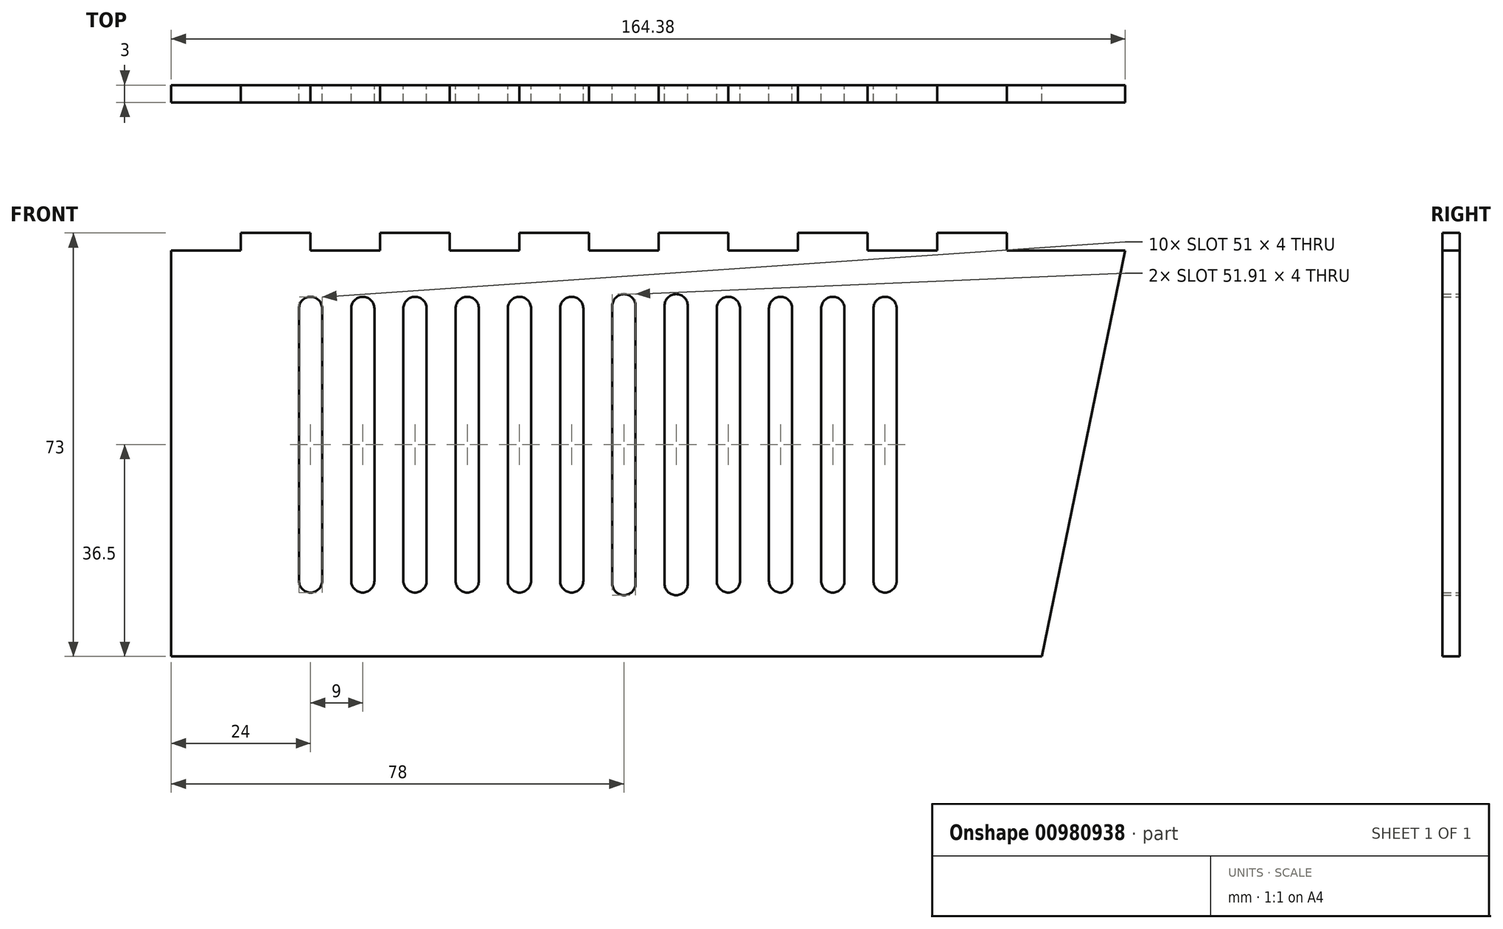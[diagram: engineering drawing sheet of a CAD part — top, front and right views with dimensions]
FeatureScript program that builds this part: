
annotation { "Feature Type Name" : "Feature", "Feature Type Description" : "" }
export const myFeature = defineFeature(function(context is Context, id is Id, definition is map)
    precondition{}
    {
        {
            var Q0;
            Q0=qCreatedBy(makeId("Front.planeOp"),FACE);
            var sketch = newSketch(context, id + "F0", { "sketchPlane" : qUnion([Q0])});
            skLineSegment(sketch, "E0.bottom", {"start": v(67.5, -36.5) * mm, "end": v(-82.5, -36.5) * mm});
            skPoint(sketch, "E0.middle", {"position": v(0, 0) * mm});
            skLineSegment(sketch, "E1", {"start": v(81.88, 33.5) * mm, "end": v(67.5, -36.5) * mm});
            skPoint(sketch, "E0.left.start.orphan", {"position": v(85.5, -36.5) * mm});
            skLineSegment(sketch, "E2", {"start": v(-82.5, -36.5) * mm, "end": v(-82.5, 33.5) * mm});
            skLineSegment(sketch, "E3", {"start": v(-82.5, 33.5) * mm, "end": v(-70.5, 33.5) * mm});
            skLineSegment(sketch, "E4", {"start": v(-70.5, 33.5) * mm, "end": v(-70.5, 36.5) * mm});
            skLineSegment(sketch, "E5", {"start": v(-70.5, 36.5) * mm, "end": v(-58.5, 36.5) * mm});
            skLineSegment(sketch, "E6", {"start": v(-58.5, 36.5) * mm, "end": v(-58.5, 33.5) * mm});
            skLineSegment(sketch, "E7", {"start": v(-58.5, 33.5) * mm, "end": v(-46.5, 33.5) * mm});
            skLineSegment(sketch, "E8.1.0.1", {"start": v(-34.5, 33.5) * mm, "end": v(-22.5, 33.5) * mm});
            skLineSegment(sketch, "E8.1.0.2", {"start": v(-46.5, 36.5) * mm, "end": v(-34.5, 36.5) * mm});
            skLineSegment(sketch, "E8.1.0.3", {"start": v(-46.5, 33.5) * mm, "end": v(-46.5, 36.5) * mm});
            skLineSegment(sketch, "E8.1.0.4", {"start": v(-34.5, 36.5) * mm, "end": v(-34.5, 33.5) * mm});
            skLineSegment(sketch, "E8.2.0.0", {"start": v(-34.5, 33.5) * mm, "end": v(-22.5, 33.5) * mm});
            skLineSegment(sketch, "E8.2.0.1", {"start": v(-10.5, 33.5) * mm, "end": v(1.5, 33.5) * mm});
            skLineSegment(sketch, "E8.2.0.2", {"start": v(-22.5, 36.5) * mm, "end": v(-10.5, 36.5) * mm});
            skLineSegment(sketch, "E8.2.0.3", {"start": v(-22.5, 33.5) * mm, "end": v(-22.5, 36.5) * mm});
            skLineSegment(sketch, "E8.2.0.4", {"start": v(-10.5, 36.5) * mm, "end": v(-10.5, 33.5) * mm});
            skLineSegment(sketch, "E8.3.0.0", {"start": v(-10.5, 33.5) * mm, "end": v(1.5, 33.5) * mm});
            skLineSegment(sketch, "E8.3.0.1", {"start": v(13.5, 33.5) * mm, "end": v(25.5, 33.5) * mm});
            skLineSegment(sketch, "E8.3.0.2", {"start": v(1.5, 36.5) * mm, "end": v(13.5, 36.5) * mm});
            skLineSegment(sketch, "E8.3.0.3", {"start": v(1.5, 33.5) * mm, "end": v(1.5, 36.5) * mm});
            skLineSegment(sketch, "E8.3.0.4", {"start": v(13.5, 36.5) * mm, "end": v(13.5, 33.5) * mm});
            skLineSegment(sketch, "E8.4.0.0", {"start": v(13.5, 33.5) * mm, "end": v(25.5, 33.5) * mm});
            skLineSegment(sketch, "E8.4.0.1", {"start": v(37.5, 33.5) * mm, "end": v(49.5, 33.5) * mm});
            skLineSegment(sketch, "E8.4.0.2", {"start": v(25.5, 36.5) * mm, "end": v(37.5, 36.5) * mm});
            skLineSegment(sketch, "E8.4.0.3", {"start": v(25.5, 33.5) * mm, "end": v(25.5, 36.5) * mm});
            skLineSegment(sketch, "E8.4.0.4", {"start": v(37.5, 36.5) * mm, "end": v(37.5, 33.5) * mm});
            skLineSegment(sketch, "E8.5.0.0", {"start": v(37.5, 33.5) * mm, "end": v(49.5, 33.5) * mm});
            skLineSegment(sketch, "E8.5.0.2", {"start": v(49.5, 36.5) * mm, "end": v(61.5, 36.5) * mm});
            skLineSegment(sketch, "E8.5.0.3", {"start": v(49.5, 33.5) * mm, "end": v(49.5, 36.5) * mm});
            skLineSegment(sketch, "E8.5.0.4", {"start": v(61.5, 36.5) * mm, "end": v(61.5, 33.5) * mm});
            skLineSegment(sketch, "E8.direction1", {"start": v(-82.5, 33.5) * mm, "end": v(-70.5, 33.5) * mm, "construction": true});
            skLineSegment(sketch, "E9", {"start": v(61.5, 33.5) * mm, "end": v(81.88, 33.5) * mm});
            skPoint(sketch, "E10.orphan", {"position": v(82.5, 36.5) * mm});
            skPoint(sketch, "E11.orphan", {"position": v(82.5, 33.5) * mm});
            skPoint(sketch, "E12.orphan", {"position": v(-82.5, 36.5) * mm});
            skLineSegment(sketch, "E13.left", {"start": v(-38.5, 23.5) * mm, "end": v(-38.5, -23.5) * mm});
            skLineSegment(sketch, "E13.right", {"start": v(-42.5, 23.5) * mm, "end": v(-42.5, -23.5) * mm});
            skPoint(sketch, "E13.middle", {"position": v(-40.5, 0) * mm});
            skLineSegment(sketch, "E14.left", {"start": v(-29.5, -23.5) * mm, "end": v(-29.5, 23.5) * mm});
            skLineSegment(sketch, "E14.right", {"start": v(-33.5, -23.5) * mm, "end": v(-33.5, 23.5) * mm});
            skPoint(sketch, "E14.middle", {"position": v(-31.5, 0) * mm});
            skLineSegment(sketch, "E15.left", {"start": v(-20.5, -23.5) * mm, "end": v(-20.5, 23.5) * mm});
            skLineSegment(sketch, "E15.right", {"start": v(-24.5, -23.5) * mm, "end": v(-24.5, 23.5) * mm});
            skPoint(sketch, "E15.middle", {"position": v(-22.5, 0) * mm});
            skLineSegment(sketch, "E16.left", {"start": v(-11.5, -23.5) * mm, "end": v(-11.5, 23.5) * mm});
            skLineSegment(sketch, "E16.right", {"start": v(-15.5, -23.5) * mm, "end": v(-15.5, 23.5) * mm});
            skPoint(sketch, "E16.middle", {"position": v(-13.5, 0) * mm});
            skLineSegment(sketch, "E17.left", {"start": v(-2.5, -23.95) * mm, "end": v(-2.5, 23.95) * mm});
            skLineSegment(sketch, "E17.right", {"start": v(-6.5, -23.95) * mm, "end": v(-6.5, 23.95) * mm});
            skPoint(sketch, "E17.middle", {"position": v(-4.5, 0) * mm});
            skLineSegment(sketch, "E18.MirrorCS", {"start": v(24.5, -23.5) * mm, "end": v(24.5, 23.5) * mm});
            skPoint(sketch, "E19.MirrorP", {"position": v(22.5, 0) * mm});
            skPoint(sketch, "E20.MirrorP", {"position": v(13.5, 0) * mm});
            skLineSegment(sketch, "E21.MirrorCS", {"start": v(20.5, -23.5) * mm, "end": v(20.5, 23.5) * mm});
            skLineSegment(sketch, "E22.MirrorCS", {"start": v(29.5, -23.5) * mm, "end": v(29.5, 23.5) * mm});
            skLineSegment(sketch, "E23.MirrorCS", {"start": v(6.5, -23.95) * mm, "end": v(6.5, 23.95) * mm});
            skPoint(sketch, "E24.MirrorP", {"position": v(40.5, 0) * mm});
            skLineSegment(sketch, "E25.MirrorCS", {"start": v(42.5, 23.5) * mm, "end": v(42.5, -23.5) * mm});
            skLineSegment(sketch, "E26.MirrorCS", {"start": v(11.5, -23.5) * mm, "end": v(11.5, 23.5) * mm});
            skPoint(sketch, "E27.MirrorP", {"position": v(4.5, 0) * mm});
            skLineSegment(sketch, "E28.MirrorCS", {"start": v(33.5, -23.5) * mm, "end": v(33.5, 23.5) * mm});
            skLineSegment(sketch, "E29.MirrorCS", {"start": v(38.5, 23.5) * mm, "end": v(38.5, -23.5) * mm});
            skLineSegment(sketch, "E30.MirrorCS", {"start": v(15.5, -23.5) * mm, "end": v(15.5, 23.5) * mm});
            skPoint(sketch, "E31.MirrorP", {"position": v(31.5, 0) * mm});
            skLineSegment(sketch, "E32.MirrorCS", {"start": v(2.5, -23.95) * mm, "end": v(2.5, 23.95) * mm});
            skLineSegment(sketch, "E33.MirrorCS", {"start": v(-56.5, -23.5) * mm, "end": v(-56.5, 23.5) * mm});
            skLineSegment(sketch, "E34.MirrorCS", {"start": v(-51.5, 23.5) * mm, "end": v(-51.5, -23.5) * mm});
            skLineSegment(sketch, "E35.MirrorCS", {"start": v(-60.5, -23.5) * mm, "end": v(-60.5, 23.5) * mm});
            skLineSegment(sketch, "E36.MirrorCS", {"start": v(-47.5, 23.5) * mm, "end": v(-47.5, -23.5) * mm});
            skPoint(sketch, "E37.MirrorP", {"position": v(-49.5, 0) * mm});
            skLineSegment(sketch, "E38.MirrorCS", {"start": v(-60.5, -23.5) * mm, "end": v(-60.33, -23.5) * mm});
            skPoint(sketch, "E39.MirrorP", {"position": v(-58.5, 0) * mm});
            skLineSegment(sketch, "E40.MirrorCS", {"start": v(-60.5, 23.5) * mm, "end": v(-60.5, 23.5) * mm});
            skArc(sketch, "E41", {"start": v(-56.5, 23.5) * mm, "mid": v(-58.5, 25.5) * mm, "end": v(-60.5, 23.5) * mm});
            skLineSegment(sketch, "E42.trimOffspring", {"start": v(-56.5, 23.5) * mm, "end": v(-56.5, 23.5) * mm});
            skLineSegment(sketch, "E43.trimOffspring", {"start": v(-56.67, -23.5) * mm, "end": v(-56.5, -23.5) * mm});
            skArc(sketch, "E44", {"start": v(-47.5, 23.5) * mm, "mid": v(-49.5, 25.5) * mm, "end": v(-51.5, 23.5) * mm});
            skArc(sketch, "E45", {"start": v(-38.5, 23.5) * mm, "mid": v(-40.5, 25.5) * mm, "end": v(-42.5, 23.5) * mm});
            skArc(sketch, "E46", {"start": v(-29.5, 23.5) * mm, "mid": v(-31.5, 25.5) * mm, "end": v(-33.5, 23.5) * mm});
            skArc(sketch, "E47", {"start": v(-20.5, 23.5) * mm, "mid": v(-22.5, 25.5) * mm, "end": v(-24.5, 23.5) * mm});
            skArc(sketch, "E48", {"start": v(-11.5, 23.5) * mm, "mid": v(-13.5, 25.5) * mm, "end": v(-15.5, 23.5) * mm});
            skArc(sketch, "E49", {"start": v(-2.5, 23.95) * mm, "mid": v(-4.5, 25.95) * mm, "end": v(-6.5, 23.95) * mm});
            skArc(sketch, "E50", {"start": v(6.5, 23.95) * mm, "mid": v(4.5, 25.95) * mm, "end": v(2.5, 23.95) * mm});
            skArc(sketch, "E51", {"start": v(15.5, 23.5) * mm, "mid": v(13.5, 25.5) * mm, "end": v(11.5, 23.5) * mm});
            skArc(sketch, "E52", {"start": v(24.5, 23.5) * mm, "mid": v(22.5, 25.5) * mm, "end": v(20.5, 23.5) * mm});
            skArc(sketch, "E53", {"start": v(33.5, 23.5) * mm, "mid": v(31.5, 25.5) * mm, "end": v(29.5, 23.5) * mm});
            skArc(sketch, "E54", {"start": v(42.5, 23.5) * mm, "mid": v(40.5, 25.5) * mm, "end": v(38.5, 23.5) * mm});
            skPoint(sketch, "E55.orphan", {"position": v(-33.5, 23.5) * mm});
            skPoint(sketch, "E14.top.start.orphan", {"position": v(-29.5, 23.5) * mm});
            skArc(sketch, "E56.MirrorCS", {"start": v(-29.5, -23.5) * mm, "mid": v(-31.5, -25.5) * mm, "end": v(-33.5, -23.5) * mm});
            skArc(sketch, "E57.MirrorCS", {"start": v(-11.5, -23.5) * mm, "mid": v(-13.5, -25.5) * mm, "end": v(-15.5, -23.5) * mm});
            skArc(sketch, "E58.MirrorCS", {"start": v(42.5, -23.5) * mm, "mid": v(40.5, -25.5) * mm, "end": v(38.5, -23.5) * mm});
            skArc(sketch, "E59.MirrorCS", {"start": v(-47.5, -23.5) * mm, "mid": v(-49.5, -25.5) * mm, "end": v(-51.5, -23.5) * mm});
            skArc(sketch, "E60.MirrorCS", {"start": v(-38.5, -23.5) * mm, "mid": v(-40.5, -25.5) * mm, "end": v(-42.5, -23.5) * mm});
            skLineSegment(sketch, "E61.MirrorCS", {"start": v(-56.5, -23.5) * mm, "end": v(-56.5, -23.5) * mm});
            skArc(sketch, "E62.MirrorCS", {"start": v(24.5, -23.5) * mm, "mid": v(22.5, -25.5) * mm, "end": v(20.5, -23.5) * mm});
            skArc(sketch, "E63.MirrorCS", {"start": v(-20.5, -23.5) * mm, "mid": v(-22.5, -25.5) * mm, "end": v(-24.5, -23.5) * mm});
            skArc(sketch, "E64.MirrorCS", {"start": v(6.5, -23.95) * mm, "mid": v(4.5, -25.95) * mm, "end": v(2.5, -23.95) * mm});
            skLineSegment(sketch, "E65.MirrorCS", {"start": v(-60.5, -23.5) * mm, "end": v(-60.5, -23.5) * mm});
            skArc(sketch, "E66.MirrorCS", {"start": v(-2.5, -23.95) * mm, "mid": v(-4.5, -25.95) * mm, "end": v(-6.5, -23.95) * mm});
            skArc(sketch, "E67.MirrorCS", {"start": v(-56.5, -23.5) * mm, "mid": v(-58.5, -25.5) * mm, "end": v(-60.5, -23.5) * mm});
            skArc(sketch, "E68.MirrorCS", {"start": v(33.5, -23.5) * mm, "mid": v(31.5, -25.5) * mm, "end": v(29.5, -23.5) * mm});
            skPoint(sketch, "E69.MirrorP", {"position": v(-29.5, -23.5) * mm});
            skArc(sketch, "E70.MirrorCS", {"start": v(15.5, -23.5) * mm, "mid": v(13.5, -25.5) * mm, "end": v(11.5, -23.5) * mm});
            skPoint(sketch, "E71.MirrorP", {"position": v(-33.5, -23.5) * mm});
            skSolve(sketch);
        }
        {
            var Q0;
            Q0=makeQuery(id+"F0.imprint","IMPRINT",FACE,{"disambiguationData":[TD([[makeQuery(id+"F0.imprint","IMPRINT",EDGE,{"derivedFrom":sQuery(id+"F0.wireOp",EDGE,"E0.bottom")}),-1.0]])]});
            extrude(context, id + "F1", {"entities" : qUnion([Q0]), "depth" : 3 * mm, "offsetDistance" : 25 * mm});
        }
    });
